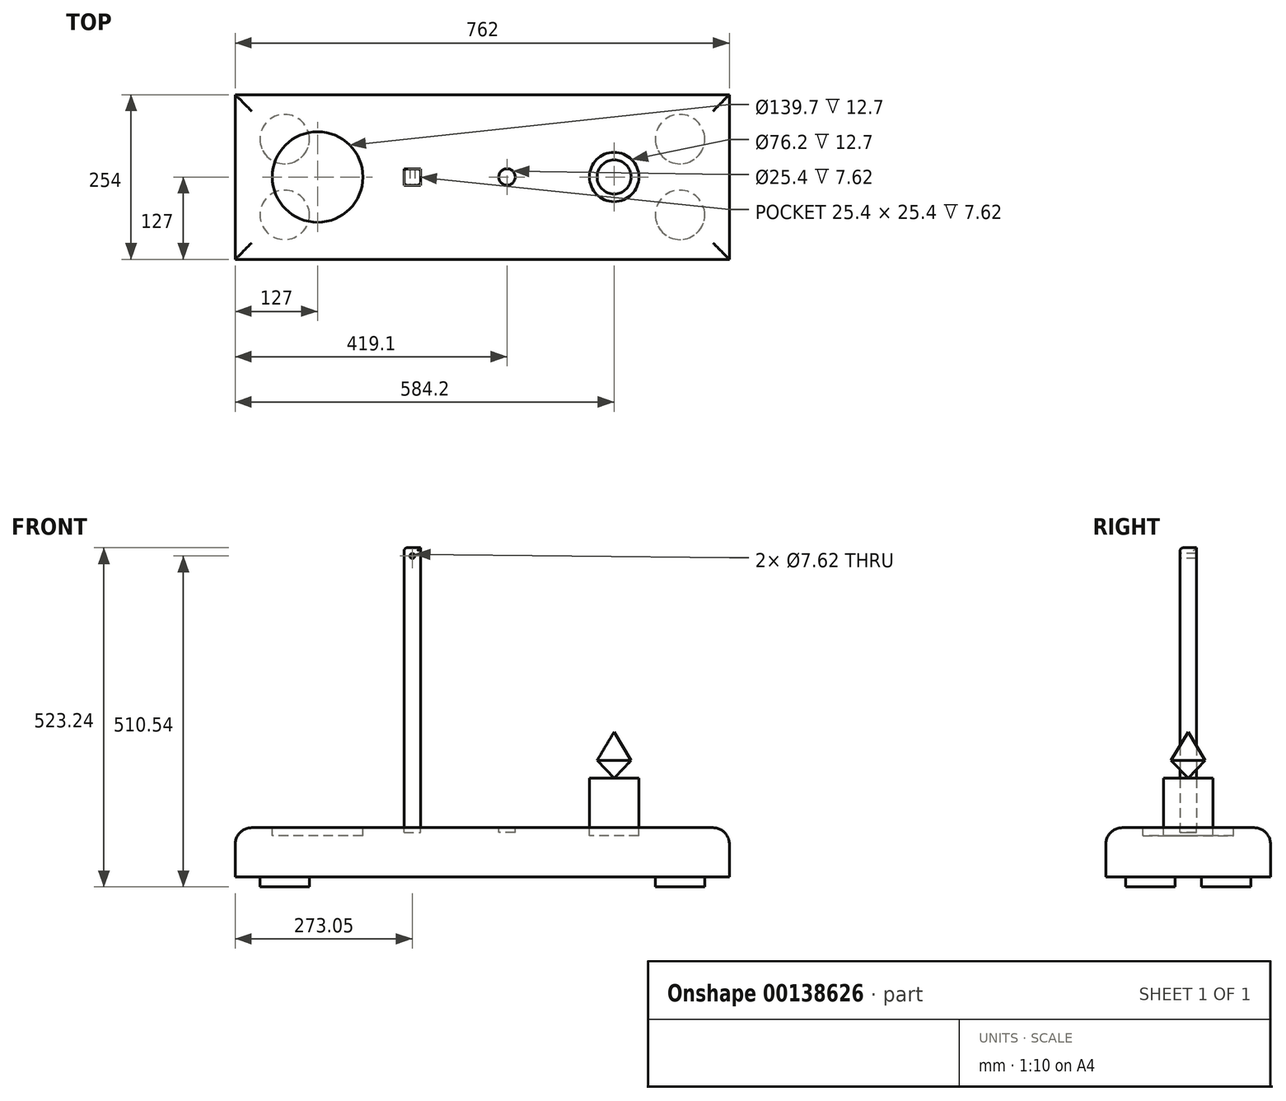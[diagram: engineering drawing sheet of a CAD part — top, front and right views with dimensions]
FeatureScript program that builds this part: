
annotation { "Feature Type Name" : "Feature", "Feature Type Description" : "" }
export const myFeature = defineFeature(function(context is Context, id is Id, definition is map)
    precondition{}
    {
        {
            var Q0;
            Q0=qCreatedBy(makeId("Front.planeOp"),FACE);
            var sketch = newSketch(context, id + "F0", { "sketchPlane" : qUnion([Q0])});
            skLineSegment(sketch, "E0.bottom", {"start": v(0, 0) * mm, "end": v(762, 0) * mm});
            skLineSegment(sketch, "E0.top", {"start": v(0, 76.2) * mm, "end": v(762, 76.2) * mm});
            skLineSegment(sketch, "E0.left", {"start": v(0, 0) * mm, "end": v(0, 76.2) * mm});
            skLineSegment(sketch, "E0.right", {"start": v(762, 0) * mm, "end": v(762, 76.2) * mm});
            skSolve(sketch);
        }
        {
            var Q0;
            Q0 = qSketchRegion(id + "F0", true);
            extrude(context, id + "F1", {"entities" : qUnion([Q0]), "depth" : 254 * mm});
        }
        {
            var Q0;
            Q0=makeQuery(id+"F1.opExtrude","SWEPT_FACE",FACE,{"disambiguationData":[OSD([sQuery(id+"F0.wireOp",EDGE,"E0.top")])]});
            var sketch = newSketch(context, id + "F2", { "sketchPlane" : qUnion([Q0])});
            skCircle(sketch, "E1", {"center": v(584.2, -127) * mm, "radius": 38.1 * mm});
            skPoint(sketch, "E1.centerSnap0", {"position": v(0, -127) * mm});
            skSolve(sketch);
        }
        {
            var Q0;
            Q0=makeQuery(id+"F1.opExtrude","SWEPT_FACE",FACE,{"disambiguationData":[OSD([sQuery(id+"F0.wireOp",EDGE,"E0.top")])]});
            var sketch = newSketch(context, id + "F3", { "sketchPlane" : qUnion([Q0])});
            skCircle(sketch, "E2", {"center": v(127, -127) * mm, "radius": 69.85 * mm});
            skSolve(sketch);
        }
        {
            var Q0;
            Q0=makeQuery(id+"F1.opExtrude","SWEPT_FACE",FACE,{"disambiguationData":[OSD([sQuery(id+"F0.wireOp",EDGE,"E0.bottom")])]});
            var sketch = newSketch(context, id + "F4", { "sketchPlane" : qUnion([Q0])});
            skCircle(sketch, "E3", {"center": v(76.2, 185.42) * mm, "radius": 38.1 * mm});
            skCircle(sketch, "E4", {"center": v(76.2, 68.58) * mm, "radius": 38.1 * mm});
            skCircle(sketch, "E5", {"center": v(685.8, 68.58) * mm, "radius": 38.1 * mm});
            skCircle(sketch, "E6", {"center": v(685.8, 185.42) * mm, "radius": 38.1 * mm});
            skSolve(sketch);
        }
        {
            var Q0;
            Q0=makeQuery(id+"F4.imprint","IMPRINT",FACE,{"disambiguationData":[TD([[makeQuery(id+"F4.imprint","IMPRINT",EDGE,{"derivedFrom":sQuery(id+"F4.wireOp",EDGE,"E3")}),1.0]])]});
            var Q1;
            Q1=makeQuery(id+"F4.imprint","IMPRINT",FACE,{"disambiguationData":[TD([[makeQuery(id+"F4.imprint","IMPRINT",EDGE,{"derivedFrom":sQuery(id+"F4.wireOp",EDGE,"E6")}),1.0]])]});
            var Q2;
            Q2=makeQuery(id+"F4.imprint","IMPRINT",FACE,{"disambiguationData":[TD([[makeQuery(id+"F4.imprint","IMPRINT",EDGE,{"derivedFrom":sQuery(id+"F4.wireOp",EDGE,"E5")}),1.0]])]});
            var Q3;
            Q3=makeQuery(id+"F4.imprint","IMPRINT",FACE,{"disambiguationData":[TD([[makeQuery(id+"F4.imprint","IMPRINT",EDGE,{"derivedFrom":sQuery(id+"F4.wireOp",EDGE,"E4")}),1.0]])]});
            extrude(context, id + "F5", {"entities" : qUnion([Q0, Q1, Q2, Q3]), "operationType" : NewBodyOperationType.ADD, "depth" : 15.24 * mm});
        }
        {
            var Q0;
            Q0=makeQuery(id+"F2.imprint","IMPRINT",FACE,{"disambiguationData":[TD([[makeQuery(id+"F2.imprint","IMPRINT",EDGE,{"derivedFrom":sQuery(id+"F2.wireOp",EDGE,"E1")}),1.0]])]});
            extrude(context, id + "F6", {"entities" : qUnion([Q0]), "depth" : 76.2 * mm});
        }
        {
            var Q0;
            Q0=makeQuery(id+"F3.imprint","IMPRINT",FACE,{"disambiguationData":[TD([[makeQuery(id+"F3.imprint","IMPRINT",EDGE,{"derivedFrom":sQuery(id+"F3.wireOp",EDGE,"E2")}),1.0]])]});
            extrude(context, id + "F7", {"entities" : qUnion([Q0]), "operationType" : NewBodyOperationType.REMOVE, "oppositeDirection" : true, "depth" : 12.7 * mm});
        }
        {
            var Q0;
            Q0 = qSketchRegion(id + "F2", true);
            extrude(context, id + "F8", {"entities" : qUnion([Q0]), "operationType" : NewBodyOperationType.REMOVE, "oppositeDirection" : true, "depth" : 12.7 * mm});
        }
        {
            var Q0;
            Q0=makeQuery(id+"F1.opExtrude","SWEPT_FACE",FACE,{"disambiguationData":[OSD([sQuery(id+"F0.wireOp",EDGE,"E0.top")])]});
            var sketch = newSketch(context, id + "F9", { "sketchPlane" : qUnion([Q0])});
            skCircle(sketch, "E7", {"center": v(419.1, -127) * mm, "radius": 12.7 * mm});
            skSolve(sketch);
        }
        {
            var Q0;
            Q0 = qSketchRegion(id + "F9", true);
            extrude(context, id + "F10", {"entities" : qUnion([Q0]), "operationType" : NewBodyOperationType.REMOVE, "oppositeDirection" : true, "depth" : 7.62 * mm});
        }
        {
            var Q0;
            Q0=makeQuery(id+"F6.opExtrude","CAP_FACE",FACE,{"disambiguationData":[OSD([sQuery(id+"F2.wireOp",EDGE,"E1")])],"isStart":false});
            var sketch = newSketch(context, id + "F11", { "sketchPlane" : qUnion([Q0])});
            skCircle(sketch, "E8", {"center": v(584.2, -127) * mm, "radius": 12.7 * mm});
            skSolve(sketch);
        }
        {
            var Q0;
            Q0=sQuery(id+"F11.wireOp",VERTEX,"E8.center");
            var Q1;
            Q1=makeQuery(id+"F0.imprint","IMPRINT",FACE,{"disambiguationData":[TD([[makeQuery(id+"F0.imprint","IMPRINT",EDGE,{"derivedFrom":sQuery(id+"F0.wireOp",EDGE,"E0.bottom")}),1.0]])]});
            cPlane(context, id + "F12", {"entities" : qUnion([Q0, Q1]), "cplaneType" : CPlaneType.PLANE_POINT, "offset" : 25.4 * mm, "width" : 152.4 * mm, "height" : 152.4 * mm});
        }
        {
            var Q0;
            Q0=qCreatedBy(id+"F12.planeOp",FACE);
            var sketch = newSketch(context, id + "F13", { "sketchPlane" : qUnion([Q0])});
            skLineSegment(sketch, "E9", {"start": v(584.2, 152.4) * mm, "end": v(610.44, 180.02) * mm});
            skLineSegment(sketch, "E10", {"start": v(610.44, 180.02) * mm, "end": v(584.2, 223.52) * mm});
            skLineSegment(sketch, "E11", {"start": v(584.2, 152.4) * mm, "end": v(584.2, 223.52) * mm});
            skSolve(sketch);
        }
        {
            var Q0;
            Q0 = qSketchRegion(id + "F13", true);
            var Q1;
            Q1=sQuery(id+"F13.wireOp",EDGE,"E11");
            revolve(context, id + "F14", {"entities" : qUnion([Q0]), "axis" : qUnion([Q1]), "revolveType" : RevolveType.FULL});
        }
        {
            var Q0;
            Q0=makeQuery(id+"F1.opExtrude","SWEPT_FACE",FACE,{"disambiguationData":[OSD([sQuery(id+"F0.wireOp",EDGE,"E0.top")])]});
            var sketch = newSketch(context, id + "F15", { "sketchPlane" : qUnion([Q0])});
            skLineSegment(sketch, "E12.bottom", {"start": v(260.35, -114.3) * mm, "end": v(285.75, -114.3) * mm});
            skLineSegment(sketch, "E12.top", {"start": v(260.35, -139.7) * mm, "end": v(285.75, -139.7) * mm});
            skLineSegment(sketch, "E12.left", {"start": v(260.35, -114.3) * mm, "end": v(260.35, -139.7) * mm});
            skLineSegment(sketch, "E12.right", {"start": v(285.75, -114.3) * mm, "end": v(285.75, -139.7) * mm});
            skSolve(sketch);
        }
        {
            var Q0;
            Q0 = qSketchRegion(id + "F15", true);
            extrude(context, id + "F16", {"entities" : qUnion([Q0]), "operationType" : NewBodyOperationType.REMOVE, "oppositeDirection" : true, "depth" : 7.62 * mm});
        }
        {
            var Q0;
            Q0 = qSketchRegion(id + "F15", true);
            extrude(context, id + "F17", {"entities" : qUnion([Q0]), "depth" : 431.8 * mm});
        }
        {
            var Q0;
            Q0=qCreatedBy(id+"F12.planeOp",FACE);
            var sketch = newSketch(context, id + "F18", { "sketchPlane" : qUnion([Q0])});
            skCircle(sketch, "E13", {"center": v(273.05, 495.3) * mm, "radius": 3.81 * mm});
            skSolve(sketch);
        }
        {
            var Q0;
            Q0 = qSketchRegion(id + "F18", true);
            extrude(context, id + "F19", {"entities" : qUnion([Q0]), "operationType" : NewBodyOperationType.REMOVE, "endBound" : BoundingType.SYMMETRIC, "oppositeDirection" : true, "depth" : 25.4 * mm});
        }
        {
            var Q0;
            Q0=makeQuery(id+"F1.opExtrude","CAP_EDGE",EDGE,{"disambiguationData":[OSD([sQuery(id+"F0.wireOp",EDGE,"E0.top")])],"isStart":false});
            var Q1;
            Q1=makeQuery(id+"F1.opExtrude","SWEPT_EDGE",EDGE,{"disambiguationData":[OSD([sQuery(id+"F0.wireOp",EDGE,"E0.top"),sQuery(id+"F0.wireOp",EDGE,"E0.right")])]});
            var Q2;
            Q2=makeQuery(id+"F1.opExtrude","CAP_EDGE",EDGE,{"disambiguationData":[OSD([sQuery(id+"F0.wireOp",EDGE,"E0.top")])],"isStart":true});
            var Q3;
            Q3=makeQuery(id+"F1.opExtrude","SWEPT_EDGE",EDGE,{"disambiguationData":[OSD([sQuery(id+"F0.wireOp",EDGE,"E0.top"),sQuery(id+"F0.wireOp",EDGE,"E0.left")])]});
            fillet(context, id + "F20", {"entities" : qUnion([Q0, Q1, Q2, Q3]), "radius" : 25.4 * mm, "tangentPropagation" : true, "allowEdgeOverflow" : false});
        }
        {
            var Q0;
            Q0=makeQuery(id+"F17.opExtrude","SWEPT_EDGE",EDGE,{"disambiguationData":[OSD([sQuery(id+"F15.wireOp",EDGE,"E12.top"),sQuery(id+"F15.wireOp",EDGE,"E12.right")])]});
            var Q1;
            Q1=makeQuery(id+"F17.opExtrude","CAP_EDGE",EDGE,{"disambiguationData":[OSD([sQuery(id+"F15.wireOp",EDGE,"E12.top")])],"isStart":false});
            var Q2;
            Q2=makeQuery(id+"F17.opExtrude","SWEPT_EDGE",EDGE,{"disambiguationData":[OSD([sQuery(id+"F15.wireOp",EDGE,"E12.bottom"),sQuery(id+"F15.wireOp",EDGE,"E12.right")])]});
            var Q3;
            Q3=makeQuery(id+"F17.opExtrude","CAP_EDGE",EDGE,{"disambiguationData":[OSD([sQuery(id+"F15.wireOp",EDGE,"E12.left")])],"isStart":false});
            var Q4;
            Q4=makeQuery(id+"F17.opExtrude","SWEPT_EDGE",EDGE,{"disambiguationData":[OSD([sQuery(id+"F15.wireOp",EDGE,"E12.top"),sQuery(id+"F15.wireOp",EDGE,"E12.left")])]});
            var Q5;
            Q5=makeQuery(id+"F17.opExtrude","SWEPT_EDGE",EDGE,{"disambiguationData":[OSD([sQuery(id+"F15.wireOp",EDGE,"E12.bottom"),sQuery(id+"F15.wireOp",EDGE,"E12.left")])]});
            fillet(context, id + "F21", {"entities" : qUnion([Q0, Q1, Q2, Q3, Q4, Q5]), "radius" : 5.08 * mm, "tangentPropagation" : true, "allowEdgeOverflow" : false});
        }
    });
